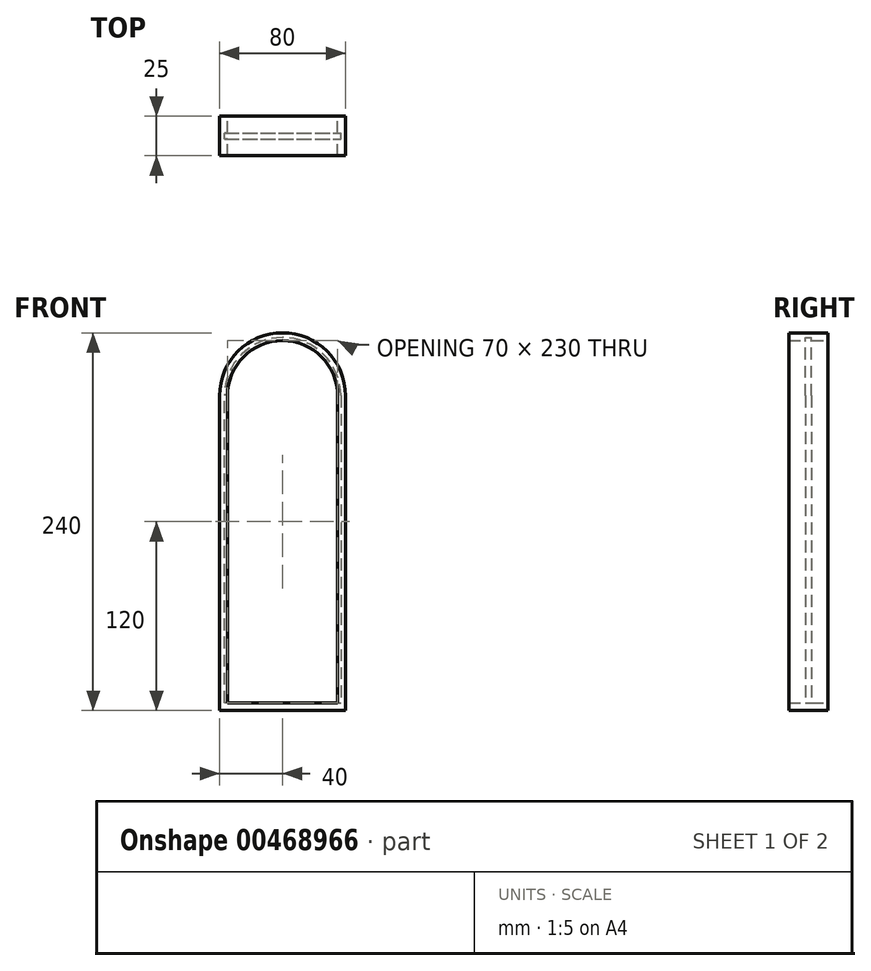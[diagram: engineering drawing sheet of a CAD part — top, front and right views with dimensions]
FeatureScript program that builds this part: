
annotation { "Feature Type Name" : "Feature", "Feature Type Description" : "" }
export const myFeature = defineFeature(function(context is Context, id is Id, definition is map)
    precondition{}
    {
        {
            var Q0;
            Q0=qCreatedBy(makeId("Front.planeOp"),FACE);
            var sketch = newSketch(context, id + "F0", { "sketchPlane" : qUnion([Q0])});
            skLineSegment(sketch, "E0.left", {"start": v(0, 0) * mm, "end": v(0, 200) * mm});
            skLineSegment(sketch, "E0.right", {"start": v(80, 0) * mm, "end": v(80, 200) * mm});
            skArc(sketch, "E1", {"start": v(80, 200) * mm, "mid": v(40, 240) * mm, "end": v(0, 200) * mm});
            skPoint(sketch, "E2.center.orphan", {"position": v(40, 0) * mm});
            skLineSegment(sketch, "E3", {"start": v(0, 0) * mm, "end": v(80, 0) * mm});
            skArc(sketch, "E4.0", {"start": v(75, 200) * mm, "mid": v(40, 235) * mm, "end": v(5, 200) * mm});
            skLineSegment(sketch, "E4.1", {"start": v(75, 5) * mm, "end": v(75, 200) * mm});
            skLineSegment(sketch, "E4.2", {"start": v(5, 5) * mm, "end": v(75, 5) * mm});
            skLineSegment(sketch, "E4.3", {"start": v(5, 5) * mm, "end": v(5, 200) * mm});
            skSolve(sketch);
        }
        {
            var Q0;
            Q0 = qSketchRegion(id + "F0", true);
            extrude(context, id + "F1", {"entities" : qUnion([Q0]), "depth" : 25 * mm});
        }
        {
            var Q0;
            Q0=makeQuery(id+"F1.opExtrude","SWEPT_FACE",FACE,{"disambiguationData":[OSD([sQuery(id+"F0.wireOp",EDGE,"E4.2")])]});
            var sketch = newSketch(context, id + "F2", { "sketchPlane" : qUnion([Q0])});
            skLineSegment(sketch, "E5.top", {"start": v(5, -10.5) * mm, "end": v(3, -10.5) * mm});
            skLineSegment(sketch, "E5.left", {"start": v(5, -12.5) * mm, "end": v(5, -10.5) * mm});
            skLineSegment(sketch, "E5.right", {"start": v(3, -12.5) * mm, "end": v(3, -10.5) * mm});
            skLineSegment(sketch, "E6.top", {"start": v(5, -14.5) * mm, "end": v(3, -14.5) * mm});
            skLineSegment(sketch, "E6.left", {"start": v(5, -12.5) * mm, "end": v(5, -14.5) * mm});
            skLineSegment(sketch, "E6.right", {"start": v(3, -12.5) * mm, "end": v(3, -14.5) * mm});
            skSolve(sketch);
        }
        {
            var Q0;
            Q0=makeQuery(id+"F2.imprint","IMPRINT",FACE,{"disambiguationData":[TD([[makeQuery(id+"F2.imprint","IMPRINT",EDGE,{"derivedFrom":sQuery(id+"F2.wireOp",EDGE,"E5.top")}),1.0]])]});
            var Q1;
            Q1=makeQuery(id+"F1.opExtrude","CAP_EDGE",EDGE,{"disambiguationData":[OSD([sQuery(id+"F0.wireOp",EDGE,"E4.3")])],"isStart":false});
            var Q2;
            Q2=makeQuery(id+"F1.opExtrude","CAP_EDGE",EDGE,{"disambiguationData":[OSD([sQuery(id+"F0.wireOp",EDGE,"E4.0")])],"isStart":false});
            var Q3;
            Q3=makeQuery(id+"F1.opExtrude","CAP_EDGE",EDGE,{"disambiguationData":[OSD([sQuery(id+"F0.wireOp",EDGE,"E4.1")])],"isStart":false});
            sweep(context, id + "F3", {"operationType" : NewBodyOperationType.REMOVE, "profiles" : qUnion([Q0]), "path" : qUnion([Q1, Q2, Q3])});
        }
    });
